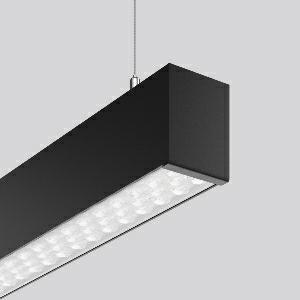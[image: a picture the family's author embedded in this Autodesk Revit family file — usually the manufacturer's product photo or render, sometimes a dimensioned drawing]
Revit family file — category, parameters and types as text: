
# Revit family: linedo_single_ip20_312564_003_1_76_6bb7
name_source: partatom
category: Lighting Fixtures
units: mm (PartAtom-declared; Revit-internal decimal feet)

## family parameters
Cut with Voids When Loaded = No
Host = Face
Light Source = No
Part Type = Normal
Room Calculation Point = No
Round Connector Dimension = Use Diameter
Shared = No

## types (1)
- LINEDO single IP20 (1 x LED Modul 840, 6450 lm, 4000)
    Apparent Load = 40 VA
    CIE Flux Codes = 86 96 99 100 100
    Color Rendering = 80
    Color Temperature = 4000
    Default Elevation = 1800 mm
    Description = Series: LINEDO single IP20
Stylish pendant luminaire. Housing: extruded aluminium profile, powder-coated. End cap aluminium powder-coated, without visible screws. High-efficiency LED units with optimum light control thanks to clear plastic (PC) lens optics. 2-point steel cable suspension freely positionable and infinitely height-adjustable. With power cord (2.5 m). Please order canopy separately if required. Perfect for office areas (RUG < 19) and environments with computer screens in accordance with EN 12464-1. 
Colour: deep black, matt (RAL 9005)
Length: 2264 mm
Width: 58 mm
Height: 76 mm
Suspension length: 100-1500 mm
Lamp: LED
Socket: without socket
Colour temperature: 4000K
Colour rendering index (CRI): 80
System power: 40 W
Rated luminous flux: 6450 lm
Beam angle Down: 59°
Luminous efficiency: 161 lm/W
Control gear: Converter, dimmable, DALI
Protection class: I
Type of protection: IP 20
    Height = 76 mm
    Lamp = 1 x LED Modul 840
    Lamp Light Flux = 6450 lm
    Lamp count = 1
    Length = 2264 mm
    Lifetime = 50000 h
    Luminous efficacy = 161 lm/W
    Manufacturer = RZB
    ModVariant = No
    Model = 312564.003.1.76
    Mounting Place = Ceiling
    Mounting Type = Surface mounted, Pendant
    Number of Poles = 1
    OnlyDefault = Yes
    Power Factor = 1
    Product Name = LINEDO single IP20
    Product group = Pendant luminaires
    ProductGroupID = 902
    Protection Class = Protection class I
    Protection Degree = IP 20
    RLX_Detail_Level = 1
    RLX_Emergency_Light_Flux = 0 lm
    RLX_Emergency_Type = 0
    RLX_Emergency_Type_DB = No
    RlxData = <blob elided: 35033 chars, md5=7b593146>
    Socket = socket
    Standby Power = 0 W
    System Light Flux = 6450 lm
    System Power = 40 W
    Type Comments = ALEA SPOT
    Type Image = 312563.003.jpg
    URL = http://relux.com
    VarID = ---
    Voltage = 230 V
    Voltage Range = 220-240 V
    Weight = 0.00 kg
    Width = 58 mm

## geometry (parser evidence)
native form markers: Blend x4, Sweep x11
no freeform markers — native parametric forms only
